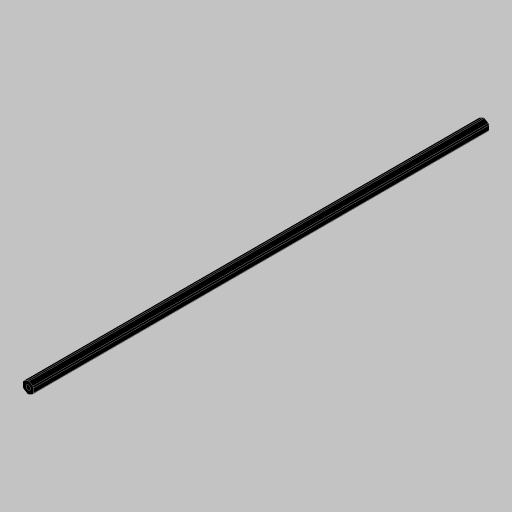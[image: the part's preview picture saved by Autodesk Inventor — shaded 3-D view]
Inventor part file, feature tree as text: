
AUTODESK INVENTOR PART (.ipt)
format: ipt  version: 2023.5 (Build 275446000, 446)  size: 117,248 bytes
history: native  units: in
note: dims shown in document units (in); Inventor stores cm internally (conversion verified against a paired STEP export)
features: extrude x2, projected_geometry x2, hole x1
ambient origin geometry x8: Origin, YZ Plane, XZ Plane, XY Plane, X Axis, Y Axis, Z Axis, Center Point
bodies: Solid1 (feature_tree)
feature tree (5):
  extrude  "Extrusion1"  TaperAngle=0.0deg  [1 undecoded]
  hole  "Hole1"  [1 undecoded]
  extrude  "Extrusion3"  TaperAngle=0.0deg  [1 undecoded]
  projected_geometry  "Project Cut Edges1"
  projected_geometry  "Project Cut Edges2"
note: 3 required parameter values undecoded (feature->parameter linkage not recoverable at this tier; creation-order binding heuristic only, values carry confidence <= 0.55)
